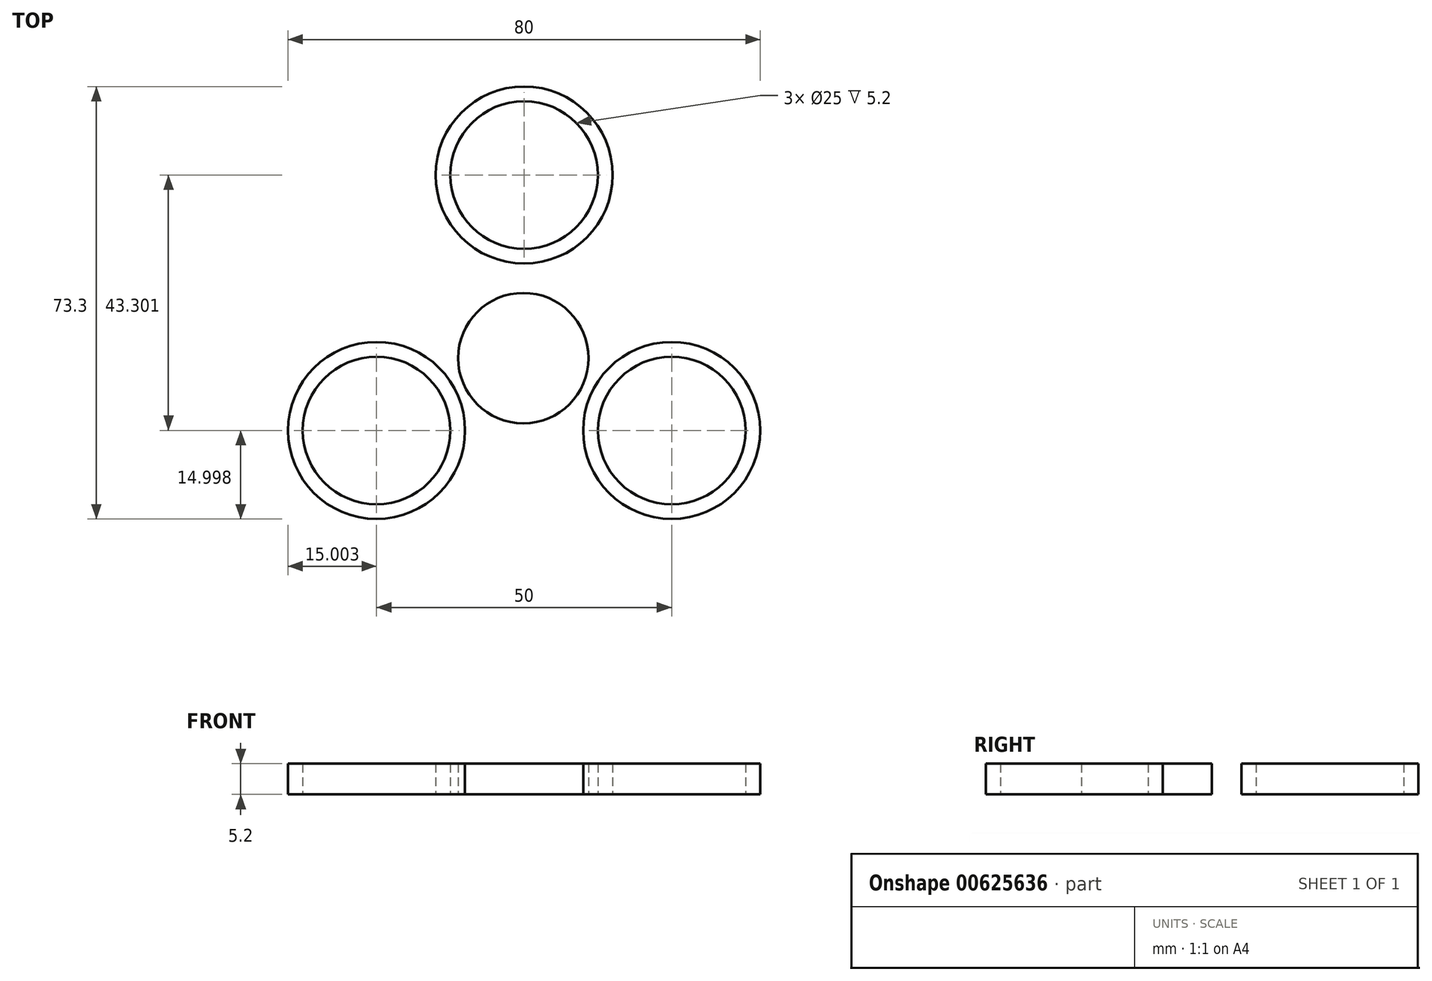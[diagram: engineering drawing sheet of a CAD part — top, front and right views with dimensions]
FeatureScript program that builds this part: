
annotation { "Feature Type Name" : "Feature", "Feature Type Description" : "" }
export const myFeature = defineFeature(function(context is Context, id is Id, definition is map)
    precondition{}
    {
        {
            var Q0;
            Q0=qCreatedBy(makeId("Top.planeOp"),FACE);
            var sketch = newSketch(context, id + "F0", { "sketchPlane" : qUnion([Q0])});
            skCircle(sketch, "E0", {"center": v(-0.09, 31.04) * mm, "radius": 12.5 * mm});
            skCircle(sketch, "E1", {"center": v(-0.09, 31.04) * mm, "radius": 15 * mm});
            skCircle(sketch, "E2", {"center": v(-25.09, -12.26) * mm, "radius": 12.5 * mm});
            skCircle(sketch, "E3", {"center": v(-25.09, -12.26) * mm, "radius": 15 * mm});
            skCircle(sketch, "E4", {"center": v(24.91, -12.26) * mm, "radius": 12.5 * mm});
            skCircle(sketch, "E5", {"center": v(24.91, -12.26) * mm, "radius": 15 * mm});
            skCircle(sketch, "E6", {"center": v(-0.22, 0) * mm, "radius": 11.05 * mm});
            skLineSegment(sketch, "E7", {"start": v(-0.09, 31.04) * mm, "end": v(-25.09, -12.26) * mm, "construction": true});
            skLineSegment(sketch, "E8", {"start": v(24.91, -12.26) * mm, "end": v(-0.09, 31.04) * mm, "construction": true});
            skLineSegment(sketch, "E9", {"start": v(-25.09, -12.26) * mm, "end": v(24.91, -12.26) * mm, "construction": true});
            skArc(sketch, "E10", {"start": v(-16.45, 0) * mm, "mid": v(-9.57, 7.8) * mm, "end": v(-7.52, 18.01) * mm});
            skLineSegment(sketch, "E11", {"start": v(-0.09, 31.04) * mm, "end": v(-0.22, -12.26) * mm, "construction": true});
            skArc(sketch, "E12.MirrorCS", {"start": v(16.09, -0.1) * mm, "mid": v(9.26, 7.75) * mm, "end": v(7.27, 17.97) * mm});
            skLineSegment(sketch, "E13.MirrorCS", {"start": v(24.66, -12.4) * mm, "end": v(-25.34, -12.11) * mm, "construction": true});
            skSolve(sketch);
        }
        {
            var Q0;
            Q0 = qSketchRegion(id + "F0", true);
            extrude(context, id + "F1", {"entities" : qUnion([Q0]), "depth" : 5.2 * mm, "offsetDistance" : 25 * mm});
        }
    });
